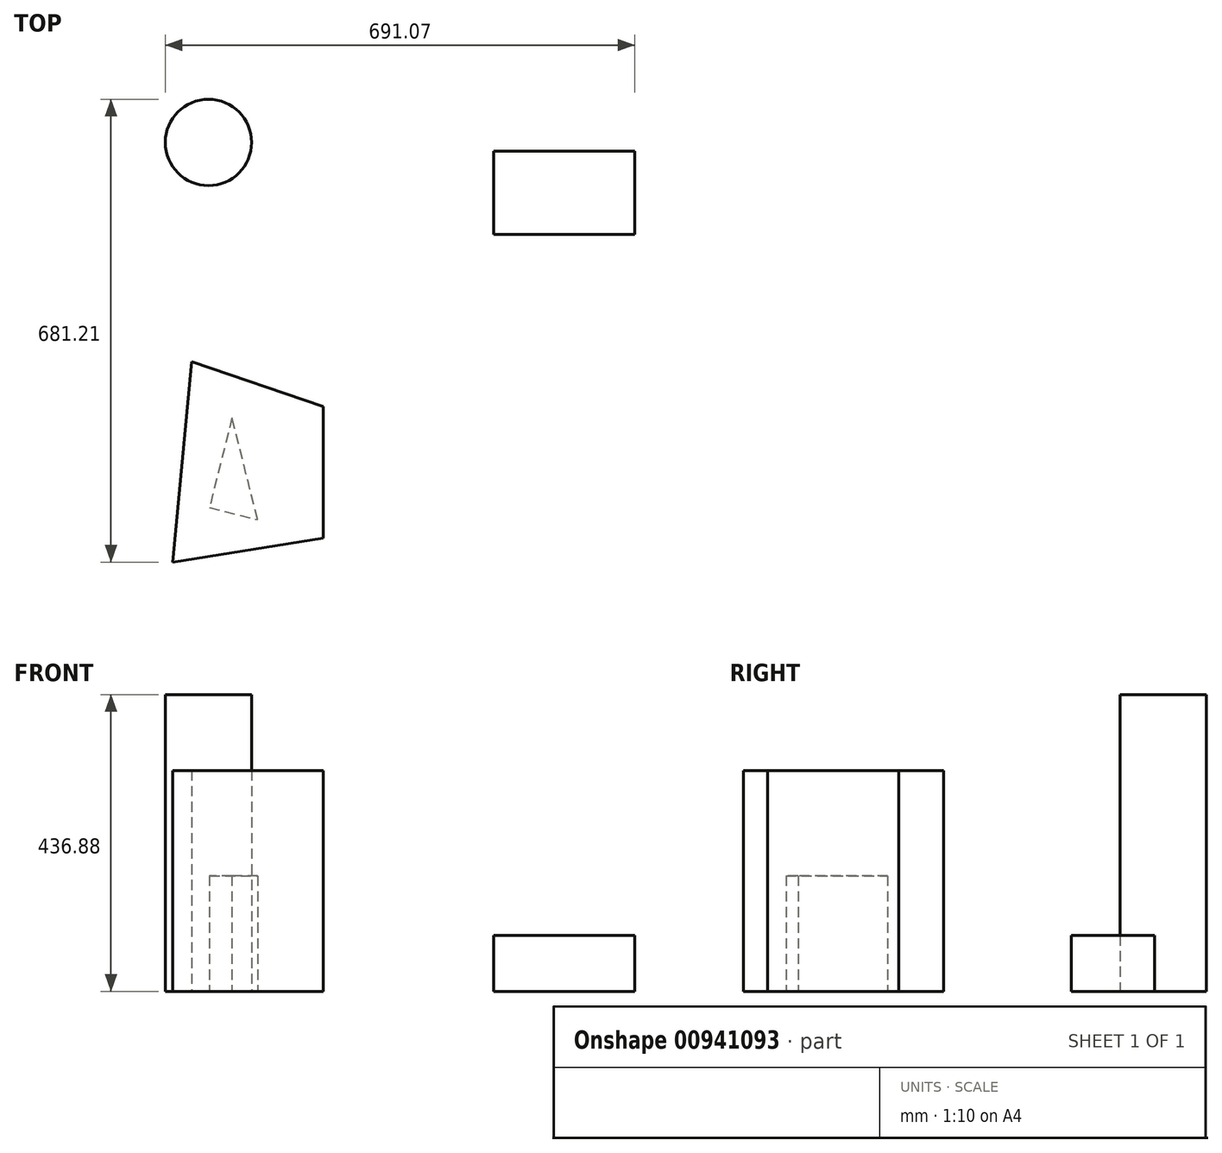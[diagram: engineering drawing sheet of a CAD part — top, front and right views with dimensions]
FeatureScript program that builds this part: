
annotation { "Feature Type Name" : "Feature", "Feature Type Description" : "" }
export const myFeature = defineFeature(function(context is Context, id is Id, definition is map)
    precondition{}
    {
        {
            var Q0;
            Q0=qCreatedBy(makeId("Top.planeOp"),FACE);
            var sketch = newSketch(context, id + "F0", { "sketchPlane" : qUnion([Q0])});
            skCircle(sketch, "E0", {"center": v(-311.54, 245.35) * mm, "radius": 63.5 * mm});
            skLineSegment(sketch, "E1.bottom", {"start": v(108.5, 232.64) * mm, "end": v(316.03, 232.64) * mm});
            skLineSegment(sketch, "E1.top", {"start": v(108.5, 110) * mm, "end": v(316.03, 110) * mm});
            skLineSegment(sketch, "E1.left", {"start": v(108.5, 232.64) * mm, "end": v(108.5, 110) * mm});
            skLineSegment(sketch, "E1.right", {"start": v(316.03, 232.64) * mm, "end": v(316.03, 110) * mm});
            skLineSegment(sketch, "E2", {"start": v(-335.96, -77.57) * mm, "end": v(-142.58, -143.6) * mm});
            skLineSegment(sketch, "E3", {"start": v(-142.58, -143.6) * mm, "end": v(-142.58, -336.98) * mm});
            skLineSegment(sketch, "E4", {"start": v(-142.58, -336.98) * mm, "end": v(-364.26, -372.36) * mm});
            skLineSegment(sketch, "E5", {"start": v(-364.26, -372.36) * mm, "end": v(-335.96, -77.57) * mm});
            skLineSegment(sketch, "E6", {"start": v(-277, -160.1) * mm, "end": v(-310.02, -292.17) * mm});
            skLineSegment(sketch, "E7", {"start": v(-310.02, -292.17) * mm, "end": v(-239, -309.93) * mm});
            skLineSegment(sketch, "E8", {"start": v(-239, -309.93) * mm, "end": v(-277, -160.1) * mm});
            skSolve(sketch);
        }
        {
            var Q0;
            Q0=makeQuery(id+"F0.imprint","IMPRINT",FACE,{"disambiguationData":[TD([[makeQuery(id+"F0.imprint","IMPRINT",EDGE,{"derivedFrom":sQuery(id+"F0.wireOp",EDGE,"E1.bottom")}),-1.0]])]});
            extrude(context, id + "F1", {"entities" : qUnion([Q0]), "depth" : 82.3 * mm, "offsetDistance" : 25.4 * mm});
        }
        {
            var Q0;
            Q0=makeQuery(id+"F0.imprint","IMPRINT",FACE,{"disambiguationData":[TD([[makeQuery(id+"F0.imprint","IMPRINT",EDGE,{"derivedFrom":sQuery(id+"F0.wireOp",EDGE,"E0")}),1.0]])]});
            extrude(context, id + "F2", {"entities" : qUnion([Q0]), "depth" : 436.88 * mm, "offsetDistance" : 25.4 * mm});
        }
        {
            var Q0;
            Q0=makeQuery(id+"F0.imprint","IMPRINT",FACE,{"disambiguationData":[TD([[makeQuery(id+"F0.imprint","IMPRINT",EDGE,{"derivedFrom":sQuery(id+"F0.wireOp",EDGE,"E2")}),-1.0]])]});
            var Q1;
            Q1=makeQuery(id+"F0.imprint","IMPRINT",FACE,{"disambiguationData":[TD([[makeQuery(id+"F0.imprint","IMPRINT",EDGE,{"derivedFrom":sQuery(id+"F0.wireOp",EDGE,"E6")}),1.0]])]});
            extrude(context, id + "F3", {"entities" : qUnion([Q0, Q1]), "depth" : 325.12 * mm, "offsetDistance" : 25.4 * mm});
        }
        {
            var Q0;
            Q0=makeQuery(id+"F0.imprint","IMPRINT",FACE,{"disambiguationData":[TD([[makeQuery(id+"F0.imprint","IMPRINT",EDGE,{"derivedFrom":sQuery(id+"F0.wireOp",EDGE,"E6")}),1.0]])]});
            extrude(context, id + "F4", {"entities" : qUnion([Q0]), "operationType" : NewBodyOperationType.REMOVE, "depth" : 170.18 * mm, "offsetDistance" : 25.4 * mm});
        }
    });
